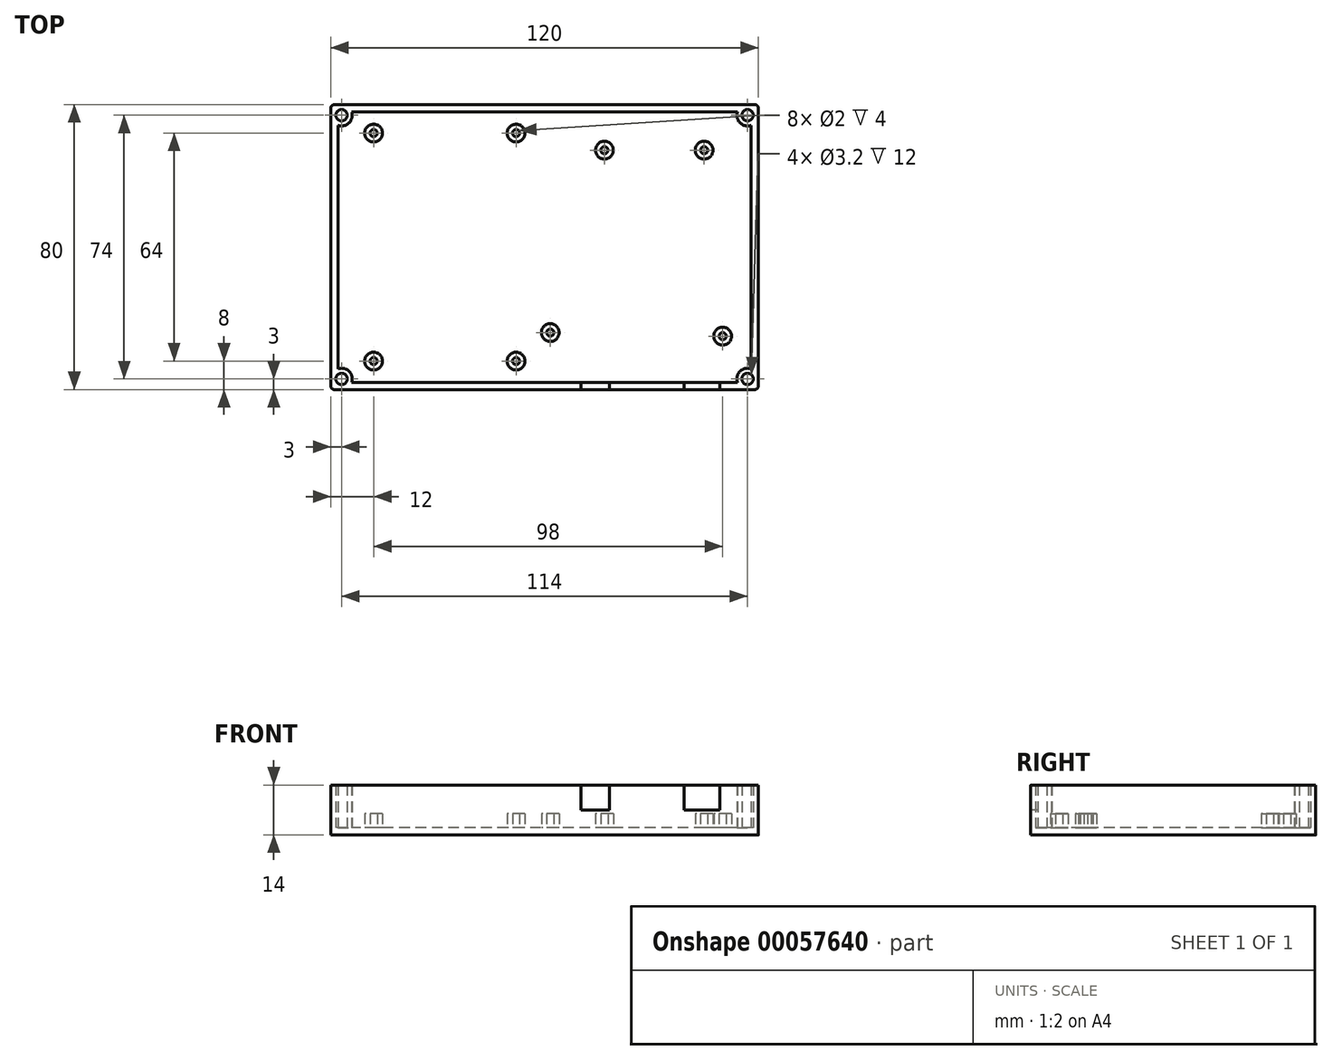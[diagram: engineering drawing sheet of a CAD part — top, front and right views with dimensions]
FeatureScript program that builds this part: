
annotation { "Feature Type Name" : "Feature", "Feature Type Description" : "" }
export const myFeature = defineFeature(function(context is Context, id is Id, definition is map)
    precondition{}
    {
        {
            var Q0;
            Q0=qCreatedBy(makeId("Top.planeOp"),FACE);
            var sketch = newSketch(context, id + "F0", { "sketchPlane" : qUnion([Q0])});
            skLineSegment(sketch, "E0.bottom", {"start": v(-60, 40) * mm, "end": v(60, 40) * mm});
            skLineSegment(sketch, "E0.top", {"start": v(-60, -40) * mm, "end": v(60, -40) * mm});
            skLineSegment(sketch, "E0.left", {"start": v(-60, 40) * mm, "end": v(-60, -40) * mm});
            skLineSegment(sketch, "E0.right", {"start": v(60, 40) * mm, "end": v(60, -40) * mm});
            skLineSegment(sketch, "E1.bottom", {"start": v(60, -40) * mm, "end": v(50, -40) * mm, "construction": true});
            skLineSegment(sketch, "E1.left", {"start": v(60, -40) * mm, "end": v(60, -25) * mm, "construction": true});
            skSolve(sketch);
        }
        {
            var Q0;
            Q0=makeQuery(id+"F0.imprint","IMPRINT",FACE,{"disambiguationData":[TD([[makeQuery(id+"F0.imprint","IMPRINT",EDGE,{"derivedFrom":sQuery(id+"F0.wireOp",EDGE,"E0.bottom")}),-1.0]])]});
            extrude(context, id + "F1", {"entities" : qUnion([Q0]), "depth" : 2 * mm});
        }
        {
            var Q0;
            Q0=makeQuery(id+"F1.opExtrude","CAP_FACE",FACE,{"disambiguationData":[OSD([sQuery(id+"F0.wireOp",EDGE,"E0.bottom"),sQuery(id+"F0.wireOp",EDGE,"E0.top"),sQuery(id+"F0.wireOp",EDGE,"E0.left"),sQuery(id+"F0.wireOp",EDGE,"E0.right")])],"isStart":false});
            var sketch = newSketch(context, id + "F2", { "sketchPlane" : qUnion([Q0])});
            skLineSegment(sketch, "E2.rect.bottom", {"start": v(58, 38) * mm, "end": v(-58, 38) * mm});
            skLineSegment(sketch, "E2.rect.top", {"start": v(58, -38) * mm, "end": v(-58, -38) * mm});
            skLineSegment(sketch, "E2.rect.left", {"start": v(58, 38) * mm, "end": v(58, -38) * mm});
            skLineSegment(sketch, "E2.rect.right", {"start": v(-58, 38) * mm, "end": v(-58, -38) * mm});
            skPoint(sketch, "E2.rect.middle", {"position": v(0, 0) * mm});
            skPoint(sketch, "E3", {"position": v(-57, 37) * mm});
            skCircle(sketch, "E4", {"center": v(-57, 37) * mm, "radius": 3 * mm});
            skPoint(sketch, "E5", {"position": v(-57, -37) * mm});
            skCircle(sketch, "E6", {"center": v(-57, -37) * mm, "radius": 3 * mm});
            skPoint(sketch, "E7", {"position": v(57, -37) * mm});
            skCircle(sketch, "E8", {"center": v(57, -37) * mm, "radius": 3 * mm});
            skPoint(sketch, "E9", {"position": v(57, 37) * mm});
            skCircle(sketch, "E10", {"center": v(57, 37) * mm, "radius": 3 * mm});
            skCircle(sketch, "E11", {"center": v(-57, -37) * mm, "radius": 1.6 * mm});
            skCircle(sketch, "E12", {"center": v(-57, 37) * mm, "radius": 1.6 * mm});
            skCircle(sketch, "E13", {"center": v(57, 37) * mm, "radius": 1.6 * mm});
            skCircle(sketch, "E14", {"center": v(57, -37) * mm, "radius": 1.6 * mm});
            skSolve(sketch);
        }
        {
            var Q0;
            {var subQ0=sQuery(id+"F2.wireOp",EDGE,"E4");var subQ1=sQuery(id+"F2.wireOp",EDGE,"E2.rect.right");var subQ2=makeQuery(id+"F2.imprint","INTERSECT",VERTEX,{"derivedFrom":[subQ1,subQ0]});Q0=makeQuery(id+"F2.imprint","IMPRINT",FACE,{"disambiguationData":[TD([[makeQuery(id+"F2.imprint","IMPRINT",EDGE,{"disambiguationData":[TD([[subQ2,-1.0]])],"derivedFrom":subQ1}),-1.0]])]});}
            var Q1;
            {var subQ0=sQuery(id+"F2.wireOp",EDGE,"E6");var subQ1=makeQuery(id+"F1.opExtrude","CAP_EDGE",EDGE,{"disambiguationData":[OSD([sQuery(id+"F0.wireOp",EDGE,"E0.left")])],"isStart":false});var subQ2=makeQuery(id+"F2.imprint","INTERSECT",VERTEX,{"derivedFrom":[subQ1,subQ0]});Q1=makeQuery(id+"F2.imprint","IMPRINT",FACE,{"disambiguationData":[TD([[makeQuery(id+"F2.imprint","IMPRINT",EDGE,{"disambiguationData":[TD([[subQ2,-1.0]])],"derivedFrom":subQ0}),-1.0]])]});}
            var Q2;
            {var subQ0=sQuery(id+"F2.wireOp",EDGE,"E6");var subQ7=sQuery(id+"F2.wireOp",EDGE,"E2.rect.top");var subQ8=makeQuery(id+"F2.imprint","INTERSECT",VERTEX,{"derivedFrom":[subQ7,subQ0]});Q2=makeQuery(id+"F2.imprint","IMPRINT",FACE,{"disambiguationData":[TD([[makeQuery(id+"F2.imprint","IMPRINT",EDGE,{"disambiguationData":[TD([[subQ8,-1.0]])],"derivedFrom":subQ7}),1.0]])]});}
            var Q3;
            {var subQ0=sQuery(id+"F2.wireOp",EDGE,"E6");var subQ1=sQuery(id+"F2.wireOp",EDGE,"E2.rect.top");var subQ2=makeQuery(id+"F2.imprint","INTERSECT",VERTEX,{"derivedFrom":[subQ1,subQ0]});Q3=makeQuery(id+"F2.imprint","IMPRINT",FACE,{"disambiguationData":[TD([[makeQuery(id+"F2.imprint","IMPRINT",EDGE,{"disambiguationData":[TD([[subQ2,-1.0]])],"derivedFrom":subQ1}),-1.0]])]});}
            var Q4;
            {var subQ0=sQuery(id+"F2.wireOp",EDGE,"E8");var subQ1=sQuery(id+"F2.wireOp",EDGE,"E2.rect.top");var subQ2=makeQuery(id+"F2.imprint","INTERSECT",VERTEX,{"derivedFrom":[subQ1,subQ0]});Q4=makeQuery(id+"F2.imprint","IMPRINT",FACE,{"disambiguationData":[TD([[makeQuery(id+"F2.imprint","IMPRINT",EDGE,{"disambiguationData":[TD([[subQ2,-1.0]])],"derivedFrom":subQ1}),1.0]])]});}
            var Q5;
            {var subQ0=sQuery(id+"F2.wireOp",EDGE,"E14");var subQ1=sQuery(id+"F2.wireOp",EDGE,"E2.rect.top");var subQ2=makeQuery(id+"F2.imprint","INTERSECT",VERTEX,{"derivedFrom":[subQ1,subQ0]});Q5=makeQuery(id+"F2.imprint","IMPRINT",FACE,{"disambiguationData":[TD([[makeQuery(id+"F2.imprint","IMPRINT",EDGE,{"disambiguationData":[TD([[subQ2,-1.0]])],"derivedFrom":subQ1}),-1.0]])]});}
            var Q6;
            {var subQ1=sQuery(id+"F2.wireOp",EDGE,"E2.rect.top");var subQ7=sQuery(id+"F2.wireOp",EDGE,"E14");var subQ9=makeQuery(id+"F2.imprint","INTERSECT",VERTEX,{"derivedFrom":[subQ1,subQ7]});Q6=makeQuery(id+"F2.imprint","IMPRINT",FACE,{"disambiguationData":[TD([[makeQuery(id+"F2.imprint","IMPRINT",EDGE,{"disambiguationData":[TD([[subQ9,-1.0]])],"derivedFrom":subQ1}),1.0]])]});}
            var Q7;
            {var subQ0=sQuery(id+"F2.wireOp",EDGE,"E8");var subQ1=makeQuery(id+"F1.opExtrude","CAP_EDGE",EDGE,{"disambiguationData":[OSD([sQuery(id+"F0.wireOp",EDGE,"E0.right")])],"isStart":false});var subQ2=makeQuery(id+"F2.imprint","INTERSECT",VERTEX,{"derivedFrom":[subQ1,subQ0]});Q7=makeQuery(id+"F2.imprint","IMPRINT",FACE,{"disambiguationData":[TD([[makeQuery(id+"F2.imprint","IMPRINT",EDGE,{"disambiguationData":[TD([[subQ2,1.0]])],"derivedFrom":subQ0}),-1.0]])]});}
            var Q8;
            {var subQ0=sQuery(id+"F2.wireOp",EDGE,"E10");var subQ1=sQuery(id+"F2.wireOp",EDGE,"E2.rect.left");var subQ2=makeQuery(id+"F2.imprint","INTERSECT",VERTEX,{"derivedFrom":[subQ1,subQ0]});Q8=makeQuery(id+"F2.imprint","IMPRINT",FACE,{"disambiguationData":[TD([[makeQuery(id+"F2.imprint","IMPRINT",EDGE,{"disambiguationData":[TD([[subQ2,-1.0]])],"derivedFrom":subQ1}),1.0]])]});}
            var Q9;
            {var subQ0=sQuery(id+"F2.wireOp",EDGE,"E13");var subQ1=sQuery(id+"F2.wireOp",EDGE,"E2.rect.bottom");var subQ2=makeQuery(id+"F2.imprint","INTERSECT",VERTEX,{"derivedFrom":[subQ1,subQ0]});Q9=makeQuery(id+"F2.imprint","IMPRINT",FACE,{"disambiguationData":[TD([[makeQuery(id+"F2.imprint","IMPRINT",EDGE,{"disambiguationData":[TD([[subQ2,-1.0]])],"derivedFrom":subQ1}),1.0]])]});}
            var Q10;
            {var subQ0=sQuery(id+"F2.wireOp",EDGE,"E10");var subQ1=sQuery(id+"F2.wireOp",EDGE,"E2.rect.bottom");var subQ2=makeQuery(id+"F2.imprint","INTERSECT",VERTEX,{"derivedFrom":[subQ1,subQ0]});Q10=makeQuery(id+"F2.imprint","IMPRINT",FACE,{"disambiguationData":[TD([[makeQuery(id+"F2.imprint","IMPRINT",EDGE,{"disambiguationData":[TD([[subQ2,-1.0]])],"derivedFrom":subQ1}),-1.0]])]});}
            var Q11;
            {var subQ1=sQuery(id+"F2.wireOp",EDGE,"E2.rect.bottom");var subQ5=sQuery(id+"F2.wireOp",EDGE,"E13");var subQ9=makeQuery(id+"F2.imprint","INTERSECT",VERTEX,{"derivedFrom":[subQ1,subQ5]});Q11=makeQuery(id+"F2.imprint","IMPRINT",FACE,{"disambiguationData":[TD([[makeQuery(id+"F2.imprint","IMPRINT",EDGE,{"disambiguationData":[TD([[subQ9,-1.0]])],"derivedFrom":subQ1}),-1.0]])]});}
            var Q12;
            {var subQ0=sQuery(id+"F2.wireOp",EDGE,"E10");var subQ1=makeQuery(id+"F1.opExtrude","CAP_EDGE",EDGE,{"disambiguationData":[OSD([sQuery(id+"F0.wireOp",EDGE,"E0.bottom")])],"isStart":false});var subQ2=makeQuery(id+"F2.imprint","INTERSECT",VERTEX,{"derivedFrom":[subQ1,subQ0]});Q12=makeQuery(id+"F2.imprint","IMPRINT",FACE,{"disambiguationData":[TD([[makeQuery(id+"F2.imprint","IMPRINT",EDGE,{"disambiguationData":[TD([[subQ2,1.0]])],"derivedFrom":subQ0}),-1.0]])]});}
            var Q13;
            {var subQ0=sQuery(id+"F2.wireOp",EDGE,"E4");var subQ1=makeQuery(id+"F1.opExtrude","CAP_EDGE",EDGE,{"disambiguationData":[OSD([sQuery(id+"F0.wireOp",EDGE,"E0.bottom")])],"isStart":false});var subQ2=makeQuery(id+"F2.imprint","INTERSECT",VERTEX,{"derivedFrom":[subQ1,subQ0]});Q13=makeQuery(id+"F2.imprint","IMPRINT",FACE,{"disambiguationData":[TD([[makeQuery(id+"F2.imprint","IMPRINT",EDGE,{"disambiguationData":[TD([[subQ2,-1.0]])],"derivedFrom":subQ0}),-1.0]])]});}
            var Q14;
            {var subQ0=sQuery(id+"F2.wireOp",EDGE,"E4");var subQ3=sQuery(id+"F2.wireOp",EDGE,"E2.rect.bottom");var subQ4=makeQuery(id+"F2.imprint","INTERSECT",VERTEX,{"derivedFrom":[subQ3,subQ0]});Q14=makeQuery(id+"F2.imprint","IMPRINT",FACE,{"disambiguationData":[TD([[makeQuery(id+"F2.imprint","IMPRINT",EDGE,{"disambiguationData":[TD([[subQ4,-1.0]])],"derivedFrom":subQ3}),-1.0]])]});}
            var Q15;
            {var subQ0=sQuery(id+"F2.wireOp",EDGE,"E4");var subQ1=sQuery(id+"F2.wireOp",EDGE,"E2.rect.bottom");var subQ2=makeQuery(id+"F2.imprint","INTERSECT",VERTEX,{"derivedFrom":[subQ1,subQ0]});Q15=makeQuery(id+"F2.imprint","IMPRINT",FACE,{"disambiguationData":[TD([[makeQuery(id+"F2.imprint","IMPRINT",EDGE,{"disambiguationData":[TD([[subQ2,-1.0]])],"derivedFrom":subQ1}),1.0]])]});}
            extrude(context, id + "F3", {"entities" : qUnion([Q0, Q1, Q2, Q3, Q4, Q5, Q6, Q7, Q8, Q9, Q10, Q11, Q12, Q13, Q14, Q15]), "operationType" : NewBodyOperationType.ADD, "depth" : 12 * mm});
        }
        {
            var Q0;
            Q0=makeQuery(id+"F1.opExtrude","CAP_FACE",FACE,{"disambiguationData":[OSD([sQuery(id+"F0.wireOp",EDGE,"E0.bottom"),sQuery(id+"F0.wireOp",EDGE,"E0.top"),sQuery(id+"F0.wireOp",EDGE,"E0.left"),sQuery(id+"F0.wireOp",EDGE,"E0.right")])],"isStart":false});
            var sketch = newSketch(context, id + "F4", { "sketchPlane" : qUnion([Q0])});
            skPoint(sketch, "E15", {"position": v(50, -25) * mm});
            skCircle(sketch, "E16", {"center": v(50, -25) * mm, "radius": 1 * mm});
            skCircle(sketch, "E17", {"center": v(50, -25) * mm, "radius": 2.5 * mm});
            skCircle(sketch, "E18", {"center": v(1.6, -24) * mm, "radius": 2.5 * mm});
            skCircle(sketch, "E19", {"center": v(1.6, -24) * mm, "radius": 1 * mm});
            skCircle(sketch, "E20", {"center": v(44.8, 27.2) * mm, "radius": 2.5 * mm});
            skCircle(sketch, "E21", {"center": v(44.8, 27.2) * mm, "radius": 1 * mm});
            skPoint(sketch, "E22", {"position": v(16.8, 27.2) * mm});
            skCircle(sketch, "E23", {"center": v(16.8, 27.2) * mm, "radius": 2.5 * mm});
            skCircle(sketch, "E24", {"center": v(16.8, 27.2) * mm, "radius": 1 * mm});
            skPoint(sketch, "E25", {"position": v(-48, 32) * mm});
            skPoint(sketch, "E26", {"position": v(-8, 32) * mm});
            skPoint(sketch, "E27", {"position": v(-8, -32) * mm});
            skPoint(sketch, "E28", {"position": v(-48, -32) * mm});
            skCircle(sketch, "E29", {"center": v(-48, 32) * mm, "radius": 1 * mm});
            skCircle(sketch, "E30", {"center": v(-8, 32) * mm, "radius": 1 * mm});
            skCircle(sketch, "E31", {"center": v(-8, -32) * mm, "radius": 1 * mm});
            skCircle(sketch, "E32", {"center": v(-48, -32) * mm, "radius": 1 * mm});
            skCircle(sketch, "E33", {"center": v(-48, 32) * mm, "radius": 2.5 * mm});
            skCircle(sketch, "E34", {"center": v(-8, 32) * mm, "radius": 2.5 * mm});
            skCircle(sketch, "E35", {"center": v(-8, -32) * mm, "radius": 2.5 * mm});
            skCircle(sketch, "E36", {"center": v(-48, -32) * mm, "radius": 2.5 * mm});
            skSolve(sketch);
        }
        {
            var Q0;
            Q0 = qSketchRegion(id + "F4", true);
            extrude(context, id + "F5", {"entities" : qUnion([Q0]), "operationType" : NewBodyOperationType.ADD, "depth" : 4 * mm});
        }
        {
            var Q0;
            {var subQ0=sQuery(id+"F0.wireOp",EDGE,"E0.top");Q0=makeQuery(id+"F3.boolean.opBoolean","MERGE",FACE,{"derivedFrom":[makeQuery(id+"F1.opExtrude","SWEPT_FACE",FACE,{"disambiguationData":[OSD([subQ0])]}),makeQuery(id+"F3.opExtrude","SWEPT_FACE",FACE,{"disambiguationData":[OSD([subQ0])]})]});}
            var sketch = newSketch(context, id + "F6", { "sketchPlane" : qUnion([Q0])});
            skLineSegment(sketch, "E37.rect.bottom", {"start": v(39.2, 7) * mm, "end": v(49.2, 7) * mm});
            skLineSegment(sketch, "E37.rect.top", {"start": v(39.2, 21) * mm, "end": v(49.2, 21) * mm});
            skLineSegment(sketch, "E37.rect.left", {"start": v(39.2, 7) * mm, "end": v(39.2, 21) * mm});
            skLineSegment(sketch, "E37.rect.right", {"start": v(49.2, 7) * mm, "end": v(49.2, 21) * mm});
            skPoint(sketch, "E37.rect.middle", {"position": v(44.2, 14) * mm});
            skLineSegment(sketch, "E38.rect.bottom", {"start": v(18.2, 21) * mm, "end": v(10.2, 21) * mm});
            skLineSegment(sketch, "E38.rect.top", {"start": v(18.2, 7) * mm, "end": v(10.2, 7) * mm});
            skLineSegment(sketch, "E38.rect.left", {"start": v(18.2, 21) * mm, "end": v(18.2, 7) * mm});
            skLineSegment(sketch, "E38.rect.right", {"start": v(10.2, 21) * mm, "end": v(10.2, 7) * mm});
            skPoint(sketch, "E38.rect.middle", {"position": v(14.2, 14) * mm});
            skSolve(sketch);
        }
        {
            var Q0;
            {var subQ0=sQuery(id+"F6.wireOp",EDGE,"E38.rect.top");Q0=makeQuery(id+"F6.imprint","IMPRINT",FACE,{"disambiguationData":[TD([[makeQuery(id+"F6.imprint","IMPRINT",EDGE,{"derivedFrom":subQ0}),-1.0]])]});}
            var Q1;
            {var subQ0=sQuery(id+"F6.wireOp",EDGE,"E37.rect.bottom");Q1=makeQuery(id+"F6.imprint","IMPRINT",FACE,{"disambiguationData":[TD([[makeQuery(id+"F6.imprint","IMPRINT",EDGE,{"derivedFrom":subQ0}),1.0]])]});}
            extrude(context, id + "F7", {"entities" : qUnion([Q0, Q1]), "operationType" : NewBodyOperationType.REMOVE, "oppositeDirection" : true, "depth" : 3 * mm});
        }
        {
            var Q0;
            {var subQ0=sQuery(id+"F0.wireOp",EDGE,"E0.right");var subQ1=sQuery(id+"F0.wireOp",EDGE,"E0.top");Q0=makeQuery(id+"F3.boolean.opBoolean","MERGE",EDGE,{"derivedFrom":[makeQuery(id+"F1.opExtrude","SWEPT_EDGE",EDGE,{"disambiguationData":[OSD([subQ1,subQ0])]}),makeQuery(id+"F3.opExtrude","SWEPT_EDGE",EDGE,{"disambiguationData":[OSD([subQ1,subQ0])]})]});}
            var Q1;
            {var subQ0=sQuery(id+"F0.wireOp",EDGE,"E0.right");var subQ1=sQuery(id+"F0.wireOp",EDGE,"E0.bottom");Q1=makeQuery(id+"F3.boolean.opBoolean","MERGE",EDGE,{"derivedFrom":[makeQuery(id+"F1.opExtrude","SWEPT_EDGE",EDGE,{"disambiguationData":[OSD([subQ1,subQ0])]}),makeQuery(id+"F3.opExtrude","SWEPT_EDGE",EDGE,{"disambiguationData":[OSD([subQ1,subQ0])]})]});}
            var Q2;
            {var subQ0=sQuery(id+"F0.wireOp",EDGE,"E0.left");var subQ1=sQuery(id+"F0.wireOp",EDGE,"E0.top");Q2=makeQuery(id+"F3.boolean.opBoolean","MERGE",EDGE,{"derivedFrom":[makeQuery(id+"F1.opExtrude","SWEPT_EDGE",EDGE,{"disambiguationData":[OSD([subQ1,subQ0])]}),makeQuery(id+"F3.opExtrude","SWEPT_EDGE",EDGE,{"disambiguationData":[OSD([subQ1,subQ0])]})]});}
            var Q3;
            {var subQ0=sQuery(id+"F0.wireOp",EDGE,"E0.left");var subQ1=sQuery(id+"F0.wireOp",EDGE,"E0.bottom");Q3=makeQuery(id+"F3.boolean.opBoolean","MERGE",EDGE,{"derivedFrom":[makeQuery(id+"F1.opExtrude","SWEPT_EDGE",EDGE,{"disambiguationData":[OSD([subQ1,subQ0])]}),makeQuery(id+"F3.opExtrude","SWEPT_EDGE",EDGE,{"disambiguationData":[OSD([subQ1,subQ0])]})]});}
            fillet(context, id + "F8", {"entities" : qUnion([Q0, Q1, Q2, Q3]), "radius" : 1 * mm, "tangentPropagation" : true, "allowEdgeOverflow" : false});
        }
    });
